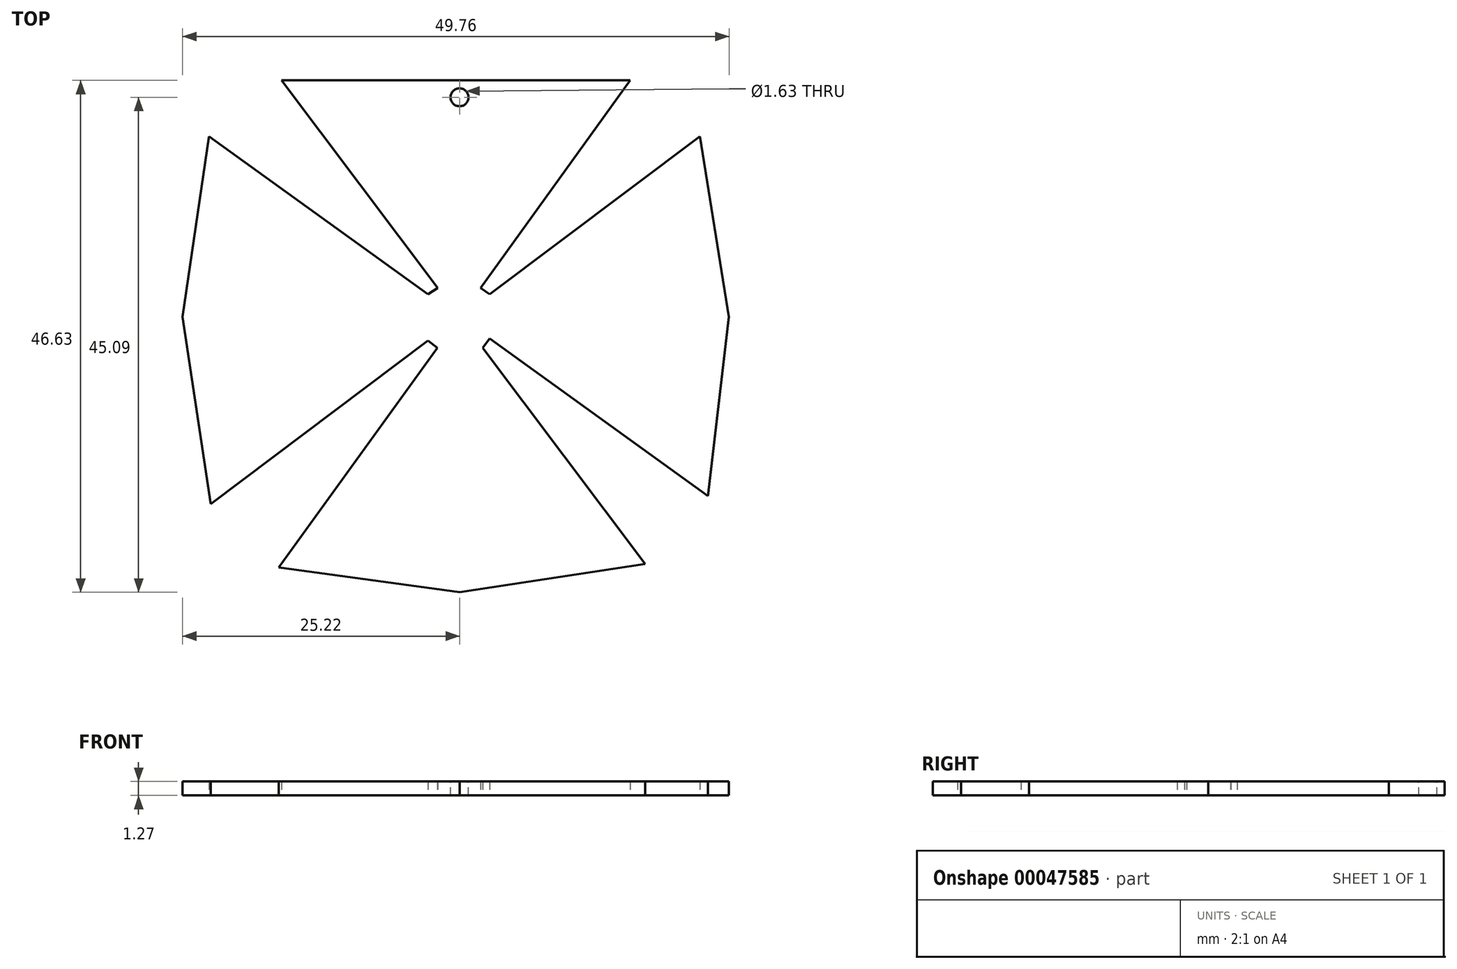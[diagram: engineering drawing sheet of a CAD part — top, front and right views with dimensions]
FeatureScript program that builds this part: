
annotation { "Feature Type Name" : "Feature", "Feature Type Description" : "" }
export const myFeature = defineFeature(function(context is Context, id is Id, definition is map)
    precondition{}
    {
        {
            var Q0;
            Q0=qCreatedBy(makeId("Top.planeOp"),FACE);
            var sketch = newSketch(context, id + "F0", { "sketchPlane" : qUnion([Q0])});
            skLineSegment(sketch, "E0", {"start": v(0, 0) * mm, "end": v(0, 29.7) * mm});
            skLineSegment(sketch, "E1", {"start": v(2.73, 2.06) * mm, "end": v(21.88, 16.45) * mm});
            skLineSegment(sketch, "E2", {"start": v(-2.87, 2.07) * mm, "end": v(-22.82, 16.45) * mm});
            skLineSegment(sketch, "E3", {"start": v(-2.03, -2.82) * mm, "end": v(-16.45, -22.83) * mm});
            skLineSegment(sketch, "E4", {"start": v(2.12, -2.82) * mm, "end": v(16.91, -22.5) * mm});
            skLineSegment(sketch, "E5", {"start": v(0, 0) * mm, "end": v(-25.22, 0) * mm});
            skLineSegment(sketch, "E6", {"start": v(0, 0) * mm, "end": v(0, -25.08) * mm});
            skLineSegment(sketch, "E7", {"start": v(0, 0) * mm, "end": v(24.54, 0) * mm});
            skLineSegment(sketch, "E8", {"start": v(1.9, 2.65) * mm, "end": v(15.53, 21.55) * mm});
            skLineSegment(sketch, "E9", {"start": v(-2, 2.65) * mm, "end": v(-16.2, 21.55) * mm});
            skLineSegment(sketch, "E10", {"start": v(-16.2, 21.55) * mm, "end": v(-22.82, 16.45) * mm});
            skLineSegment(sketch, "E11", {"start": v(15.53, 21.55) * mm, "end": v(21.88, 16.45) * mm});
            skLineSegment(sketch, "E12", {"start": v(-2.87, -2.16) * mm, "end": v(-22.67, -17.04) * mm});
            skLineSegment(sketch, "E13", {"start": v(-22.67, -17.04) * mm, "end": v(-16.45, -22.83) * mm});
            skLineSegment(sketch, "E14", {"start": v(2.73, -1.97) * mm, "end": v(22.62, -16.3) * mm});
            skLineSegment(sketch, "E15", {"start": v(22.62, -16.3) * mm, "end": v(16.91, -22.5) * mm});
            skLineSegment(sketch, "E16", {"start": v(0, -25.08) * mm, "end": v(16.91, -22.5) * mm});
            skLineSegment(sketch, "E17", {"start": v(0, -25.08) * mm, "end": v(-16.45, -22.83) * mm});
            skLineSegment(sketch, "E18", {"start": v(-22.67, -17.04) * mm, "end": v(-25.22, 0) * mm});
            skLineSegment(sketch, "E19", {"start": v(-25.22, 0) * mm, "end": v(-22.82, 16.45) * mm});
            skLineSegment(sketch, "E20", {"start": v(-16.2, 21.55) * mm, "end": v(15.53, 21.55) * mm});
            skLineSegment(sketch, "E21", {"start": v(22.62, -16.3) * mm, "end": v(24.54, 0) * mm});
            skLineSegment(sketch, "E22", {"start": v(21.88, 16.45) * mm, "end": v(24.54, 0) * mm});
            skLineSegment(sketch, "E23", {"start": v(-2.87, 2.07) * mm, "end": v(-2.87, -2.16) * mm});
            skLineSegment(sketch, "E24", {"start": v(-2.03, -2.82) * mm, "end": v(2.12, -2.82) * mm});
            skLineSegment(sketch, "E25", {"start": v(2.12, -2.82) * mm, "end": v(2.73, -1.97) * mm});
            skLineSegment(sketch, "E26", {"start": v(2.73, -1.97) * mm, "end": v(2.73, 2.06) * mm});
            skLineSegment(sketch, "E27", {"start": v(2.73, 2.06) * mm, "end": v(1.9, 2.65) * mm});
            skLineSegment(sketch, "E28", {"start": v(1.9, 2.65) * mm, "end": v(-2, 2.65) * mm});
            skLineSegment(sketch, "E29", {"start": v(-2, 2.65) * mm, "end": v(-2.87, 2.07) * mm});
            skLineSegment(sketch, "E30", {"start": v(-2.87, -2.16) * mm, "end": v(-2.03, -2.82) * mm});
            skSolve(sketch);
        }
        {
            var Q0;
            Q0=makeQuery(id+"F0.imprint","IMPRINT",FACE,{"disambiguationData":[TD([[makeQuery(id+"F0.imprint","IMPRINT",EDGE,{"derivedFrom":sQuery(id+"F0.wireOp",EDGE,"E4")}),-1.0]])]});
            var Q1;
            {var subQ3=sQuery(id+"F0.wireOp",EDGE,"E9");Q1=makeQuery(id+"F0.imprint","IMPRINT",FACE,{"disambiguationData":[TD([[makeQuery(id+"F0.imprint","IMPRINT",EDGE,{"derivedFrom":subQ3}),-1.0]])]});}
            var Q2;
            {var subQ3=sQuery(id+"F0.wireOp",EDGE,"E8");Q2=makeQuery(id+"F0.imprint","IMPRINT",FACE,{"disambiguationData":[TD([[makeQuery(id+"F0.imprint","IMPRINT",EDGE,{"derivedFrom":subQ3}),1.0]])]});}
            var Q3;
            Q3=makeQuery(id+"F0.imprint","IMPRINT",FACE,{"disambiguationData":[TD([[makeQuery(id+"F0.imprint","IMPRINT",EDGE,{"derivedFrom":sQuery(id+"F0.wireOp",EDGE,"E7")}),-1.0]])]});
            var Q4;
            Q4=makeQuery(id+"F0.imprint","IMPRINT",FACE,{"disambiguationData":[TD([[makeQuery(id+"F0.imprint","IMPRINT",EDGE,{"derivedFrom":sQuery(id+"F0.wireOp",EDGE,"E1")}),-1.0]])]});
            var Q5;
            Q5=makeQuery(id+"F0.imprint","IMPRINT",FACE,{"disambiguationData":[TD([[makeQuery(id+"F0.imprint","IMPRINT",EDGE,{"derivedFrom":sQuery(id+"F0.wireOp",EDGE,"E2")}),1.0]])]});
            var Q6;
            Q6=makeQuery(id+"F0.imprint","IMPRINT",FACE,{"disambiguationData":[TD([[makeQuery(id+"F0.imprint","IMPRINT",EDGE,{"derivedFrom":sQuery(id+"F0.wireOp",EDGE,"E5")}),1.0]])]});
            var Q7;
            Q7=makeQuery(id+"F0.imprint","IMPRINT",FACE,{"disambiguationData":[TD([[makeQuery(id+"F0.imprint","IMPRINT",EDGE,{"derivedFrom":sQuery(id+"F0.wireOp",EDGE,"E3")}),1.0]])]});
            var Q8;
            {var subQ3=sQuery(id+"F0.wireOp",EDGE,"E25");Q8=makeQuery(id+"F0.imprint","IMPRINT",FACE,{"disambiguationData":[TD([[makeQuery(id+"F0.imprint","IMPRINT",EDGE,{"derivedFrom":subQ3}),1.0]])]});}
            var Q9;
            {var subQ3=sQuery(id+"F0.wireOp",EDGE,"E27");Q9=makeQuery(id+"F0.imprint","IMPRINT",FACE,{"disambiguationData":[TD([[makeQuery(id+"F0.imprint","IMPRINT",EDGE,{"derivedFrom":subQ3}),1.0]])]});}
            var Q10;
            {var subQ5=sQuery(id+"F0.wireOp",EDGE,"E29");Q10=makeQuery(id+"F0.imprint","IMPRINT",FACE,{"disambiguationData":[TD([[makeQuery(id+"F0.imprint","IMPRINT",EDGE,{"derivedFrom":subQ5}),1.0]])]});}
            var Q11;
            {var subQ0=sQuery(id+"F0.wireOp",EDGE,"E30");Q11=makeQuery(id+"F0.imprint","IMPRINT",FACE,{"disambiguationData":[TD([[makeQuery(id+"F0.imprint","IMPRINT",EDGE,{"derivedFrom":subQ0}),1.0]])]});}
            extrude(context, id + "F1", {"entities" : qUnion([Q0, Q1, Q2, Q3, Q4, Q5, Q6, Q7, Q8, Q9, Q10, Q11]), "depth" : 1.27 * mm});
        }
        {
            var Q0;
            Q0=makeQuery(id+"F1.opExtrude","CAP_FACE",FACE,{"disambiguationData":[OSD([sQuery(id+"F0.wireOp",EDGE,"E8"),sQuery(id+"F0.wireOp",EDGE,"E9"),sQuery(id+"F0.wireOp",EDGE,"E20")])],"isStart":false});
            var sketch = newSketch(context, id + "F2", { "sketchPlane" : qUnion([Q0])});
            skCircle(sketch, "E31", {"center": v(0, 20.01) * mm, "radius": 0.82 * mm});
            skSolve(sketch);
        }
        {
            var Q0;
            Q0 = qSketchRegion(id + "F2", true);
            extrude(context, id + "F3", {"entities" : qUnion([Q0]), "operationType" : NewBodyOperationType.REMOVE, "oppositeDirection" : true, "depth" : 12.7 * mm});
        }
    });
